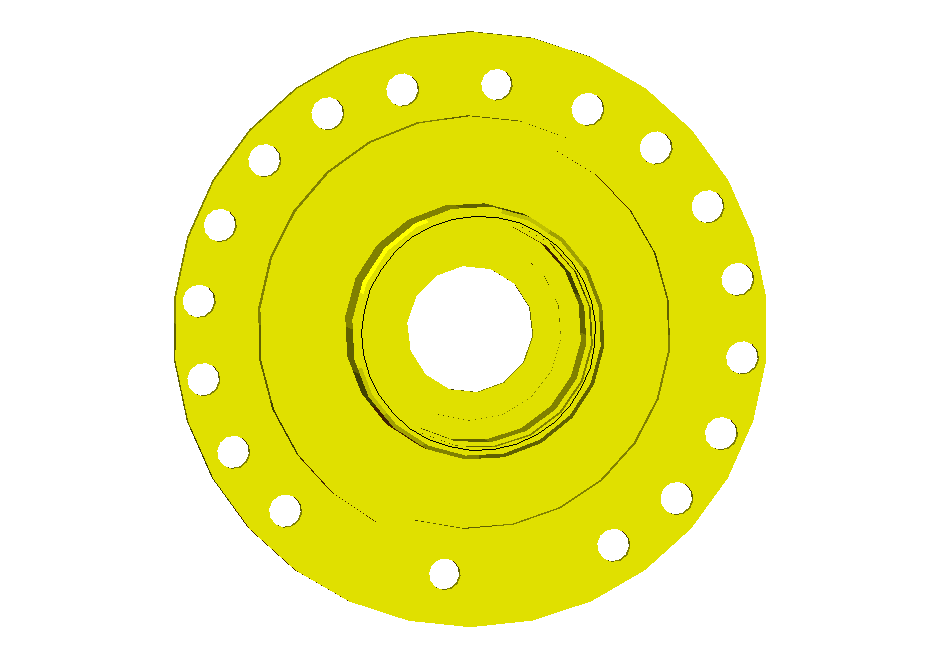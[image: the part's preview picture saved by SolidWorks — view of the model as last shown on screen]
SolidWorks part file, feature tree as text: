
SOLIDWORKS PART (.sldprt)
format: sldprt  version: not decoded by parser v0  size: 274,944 bytes
history: native  units: mm
features: sketch x6, pattern_circular x4, cut_extrude x3, revolve x1, thread x1, chamfer x1 (+8 scaffold rows collapsed)
feature tree (24):
  scaffold x8  (default folders/planes/origin — collapsed)
  sketch  "Sketch1"  dims[c1.D1=29.5mm c1.D2=2.5mm c1.D3=10.5mm c1.D4=3.5mm c1.D5=2.0mm c1.D6=3.0mm c1.D7=9.0mm c1.D8=12.0mm c1.D9=1.5mm c1.D10=3.0mm c1.D11=0.25mm c1.D12=1.0mm c1.D13=0.5mm c1.D14=9.0mm c1.D15=2.5mm c1.D16=0.5mm c1.D17=3.5mm c2.D13=0.75mm c2.D17=3.5mm c2.D18=1.5mm c2.D19=8.0mm]
  revolve  "Base-Revolve"  [1 undecoded]
  thread  "Cosmetic Thread4"  Diameter=3mm  [1 undecoded]
  sketch  "Sketch2"  dims[c1.D5=4.2mm c1.D6=4.2mm c1.D9=4.0mm c1.D10=4.0mm c1.D1=4.5mm c1.D2=30.0mm c1.D3=4.5mm c1.D4=30.0mm c2.D5=~30.020491mm c2.D7=31.0mm c2.D8=31.0mm c2.D11=1.5mm c2.D12=3.0mm c3.D11=1.5mm c3.D12=3.0mm]
  sketch  "Sketch6"
  sketch  "Sketch5"
  sketch  "Sketch4"
  sketch  "Sketch3"
  cut_extrude  "Cut-Extrude1"  Depth=10mm
  pattern_circular  "CirPattern1"  Count=4 Angle=57deg
  pattern_circular  "CirPattern2"  Count=5 Angle=76deg
  cut_extrude  "Cut-Extrude2"  Depth=10mm
  pattern_circular  "CirPattern3"  Count=5 Angle=76deg
  pattern_circular  "CirPattern4"  Count=4 Angle=57deg
  cut_extrude  "Cut-Extrude3"  Depth=10mm
  chamfer  "Chamfer1"  Distance=0.5mm Angle=45deg
decode coverage: 11 of 16 modeling features carry decoded parameters
note: ~ marks probable driven/reference dimensions
note: 2 parameter values undecoded
note: suppression state not decoded; provenance and decode notes live in map.json
